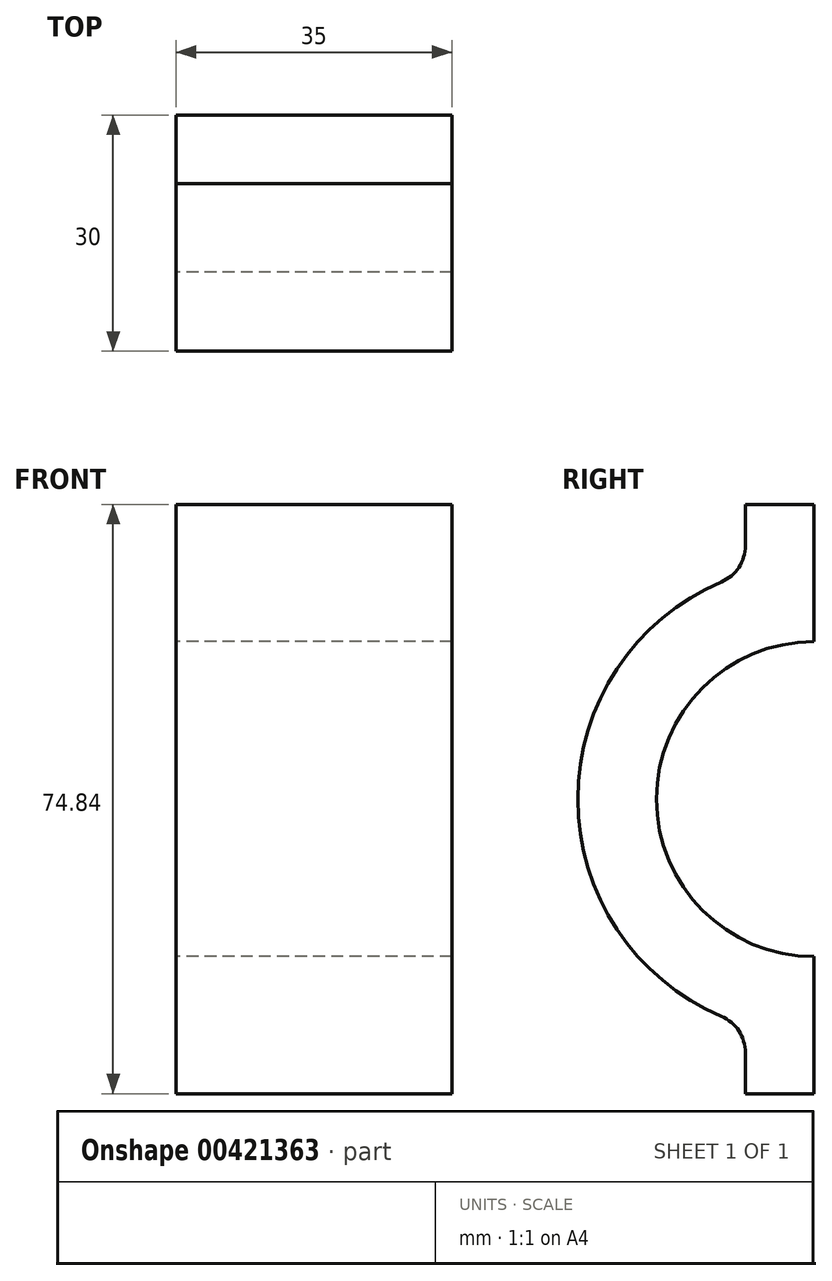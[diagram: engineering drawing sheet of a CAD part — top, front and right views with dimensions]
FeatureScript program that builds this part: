
annotation { "Feature Type Name" : "Feature", "Feature Type Description" : "" }
export const myFeature = defineFeature(function(context is Context, id is Id, definition is map)
    precondition{}
    {
        {
            var Q0;
            Q0=qCreatedBy(makeId("Right.planeOp"),FACE);
            var sketch = newSketch(context, id + "F0", { "sketchPlane" : qUnion([Q0])});
            skArc(sketch, "E0", {"start": v(0, 20) * mm, "mid": v(-20, 0) * mm, "end": v(0, -20) * mm});
            skLineSegment(sketch, "E1", {"start": v(0, 20) * mm, "end": v(0, 37.42) * mm});
            skLineSegment(sketch, "E2", {"start": v(0, 37.42) * mm, "end": v(-8.7, 37.42) * mm});
            skLineSegment(sketch, "E3", {"start": v(-8.7, 37.42) * mm, "end": v(-8.7, 28.7) * mm});
            skLineSegment(sketch, "E4", {"start": v(0, -20) * mm, "end": v(0, -37.42) * mm});
            skLineSegment(sketch, "E5", {"start": v(0, -37.42) * mm, "end": v(-8.7, -37.42) * mm});
            skLineSegment(sketch, "E6", {"start": v(-8.7, -37.42) * mm, "end": v(-8.7, -28.7) * mm});
            skLineSegment(sketch, "E7", {"start": v(-8.7, 28.7) * mm, "end": v(0, 28.7) * mm, "construction": true});
            skLineSegment(sketch, "E8", {"start": v(-8.7, -28.7) * mm, "end": v(0, -28.7) * mm, "construction": true});
            skArc(sketch, "E9", {"start": v(-8.7, 28.7) * mm, "mid": v(-30, 0) * mm, "end": v(-8.7, -28.7) * mm});
            skSolve(sketch);
        }
        {
            var Q0;
            Q0=makeQuery(id+"F0.imprint","IMPRINT",FACE,{"disambiguationData":[TD([[makeQuery(id+"F0.imprint","IMPRINT",EDGE,{"derivedFrom":sQuery(id+"F0.wireOp",EDGE,"E0")}),-1.0]])]});
            extrude(context, id + "F1", {"entities" : qUnion([Q0]), "depth" : 35 * mm});
        }
        {
            var Q0;
            Q0=makeQuery(id+"F1.opExtrude","SWEPT_EDGE",EDGE,{"disambiguationData":[OSD([sQuery(id+"F0.wireOp",EDGE,"E3"),sQuery(id+"F0.wireOp",EDGE,"E9")])]});
            var Q1;
            Q1=makeQuery(id+"F1.opExtrude","SWEPT_EDGE",EDGE,{"disambiguationData":[OSD([sQuery(id+"F0.wireOp",EDGE,"E6"),sQuery(id+"F0.wireOp",EDGE,"E9")])]});
            fillet(context, id + "F2", {"entities" : qUnion([Q0, Q1]), "radius" : 5 * mm, "tangentPropagation" : true, "allowEdgeOverflow" : false});
        }
    });
